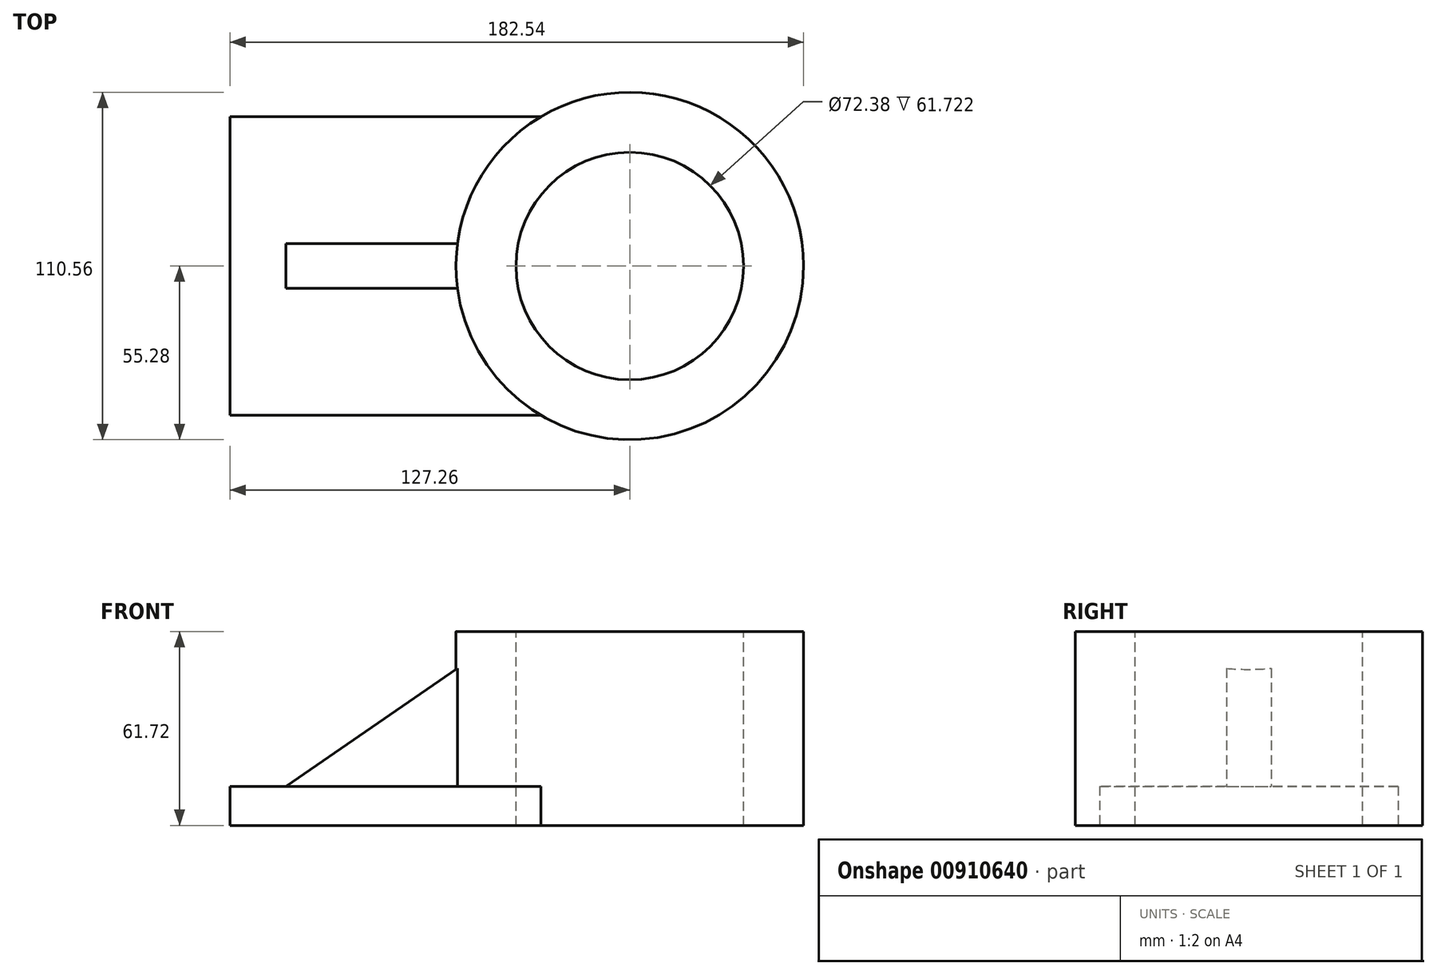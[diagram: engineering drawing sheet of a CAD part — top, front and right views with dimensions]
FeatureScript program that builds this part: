
annotation { "Feature Type Name" : "Feature", "Feature Type Description" : "" }
export const myFeature = defineFeature(function(context is Context, id is Id, definition is map)
    precondition{}
    {
        {
            var Q0;
            Q0=qCreatedBy(makeId("Top.planeOp"),FACE);
            var sketch = newSketch(context, id + "F0", { "sketchPlane" : qUnion([Q0])});
            skLineSegment(sketch, "E0.bottom", {"start": v(71.98, -47.5) * mm, "end": v(-71.98, -47.5) * mm});
            skLineSegment(sketch, "E0.top", {"start": v(71.98, 47.5) * mm, "end": v(-71.98, 47.5) * mm});
            skLineSegment(sketch, "E0.left", {"start": v(71.98, -47.5) * mm, "end": v(71.98, 47.5) * mm});
            skLineSegment(sketch, "E0.right", {"start": v(-71.98, -47.5) * mm, "end": v(-71.98, 47.5) * mm});
            skPoint(sketch, "E0.middle", {"position": v(0, 0) * mm});
            skSolve(sketch);
        }
        {
            var Q0;
            Q0=qSketchRegion(id+"F0",true);
            extrude(context, id + "F1", {"entities" : qUnion([Q0]), "depth" : 12.45 * mm});
        }
        {
            var Q0;
            Q0=qCreatedBy(makeId("Top.planeOp"),FACE);
            var sketch = newSketch(context, id + "F2", { "sketchPlane" : qUnion([Q0])});
            skCircle(sketch, "E1", {"center": v(55.28, 0) * mm, "radius": 55.28 * mm});
            skSolve(sketch);
        }
        {
            var Q0;
            Q0=makeQuery(id+"F2.imprint","IMPRINT",FACE,{"disambiguationData":[TD([[makeQuery(id+"F2.imprint","IMPRINT",EDGE,{"derivedFrom":sQuery(id+"F2.wireOp",EDGE,"E1")}),1.0]])]});
            extrude(context, id + "F3", {"entities" : qUnion([Q0]), "operationType" : NewBodyOperationType.ADD, "depth" : 61.72 * mm});
        }
        {
            var Q0;
            Q0=makeQuery(id+"F3.opExtrude","CAP_FACE",FACE,{"disambiguationData":[OSD([sQuery(id+"F2.wireOp",EDGE,"E1")])],"isStart":false});
            var sketch = newSketch(context, id + "F4", { "sketchPlane" : qUnion([Q0])});
            skCircle(sketch, "E2", {"center": v(55.28, 0) * mm, "radius": 36.2 * mm});
            skSolve(sketch);
        }
        {
            var Q0;
            Q0=qSketchRegion(id+"F4",true);
            extrude(context, id + "F5", {"entities" : qUnion([Q0]), "operationType" : NewBodyOperationType.REMOVE, "endBound" : BoundingType.THROUGH_ALL, "oppositeDirection" : true, "depth" : 25.4 * mm});
        }
        {
            var Q0;
            Q0=qCreatedBy(makeId("Front.planeOp"),FACE);
            var sketch = newSketch(context, id + "F6", { "sketchPlane" : qUnion([Q0])});
            skLineSegment(sketch, "E3", {"start": v(9.26, 56.01) * mm, "end": v(-61.7, 7.27) * mm});
            skLineSegment(sketch, "E4", {"start": v(-61.7, 7.27) * mm, "end": v(9.26, 7.27) * mm});
            skLineSegment(sketch, "E5", {"start": v(9.26, 7.27) * mm, "end": v(9.26, 56.01) * mm});
            skSolve(sketch);
        }
        {
            var Q0;
            Q0=qSketchRegion(id+"F6",true);
            extrude(context, id + "F7", {"entities" : qUnion([Q0]), "operationType" : NewBodyOperationType.ADD, "endBound" : BoundingType.SYMMETRIC, "depth" : 14.22 * mm});
        }
    });
